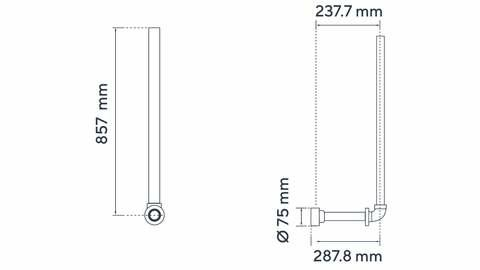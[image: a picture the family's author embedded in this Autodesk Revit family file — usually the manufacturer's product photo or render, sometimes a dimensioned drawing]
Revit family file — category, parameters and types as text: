
# Revit family: IS-CO01-211 CONEXION POSTERIOR SANITARIO
name_source: partatom
category: Aparatos sanitarios
revit_build: Autodesk Revit 2018 (Build: 20170223_1515(x64)
units: mm (PartAtom-declared; Revit-internal decimal feet)

## family parameters
Anfitrión = Cara
Compartido = No
Corte con vacíos al cargar = No
Cota de conector redondo = Diámetro de uso
Número OmniClass = 23.31.11.00
Punto de cálculo de habitación = No
Tipo de pieza = Normal

## types (1)
- IS-CO01-211
    Alto = 857 mm  [stored 2.81168 ft]
    Ancho = 287.8 mm  [stored 0.944226 ft]
    Conexión AC = Sí
    Conexión AF = Sí
    Conexión de residuos = No
    Conexión de ventilación = No
    Descripción = Conexion
    Elevación por defecto = 0 mm  [stored 0 ft]
    Fabricante = Gricol
    Imagen de tipo = Conexionposterior_540x.png
    Link Ficha Tecnica = http://infotecnica.gricol.com
    Modelo = IS-CO01-211
    PVC Blanco = PVC Blanco
    Plastico ABS Cromado = Plastico - ABS Cromado
    Product Name = CONEXION POSTERIOR SANITARIO
    Tuerca = 75 mm
    URL = https://www.gricol.com

note: [stored X ft] marks values corroborated as IEEE doubles in the binary element streams (Revit-internal decimal feet)

## geometry (parser evidence)
native form markers: Blend x2, Sweep x5
no freeform markers — native parametric forms only
